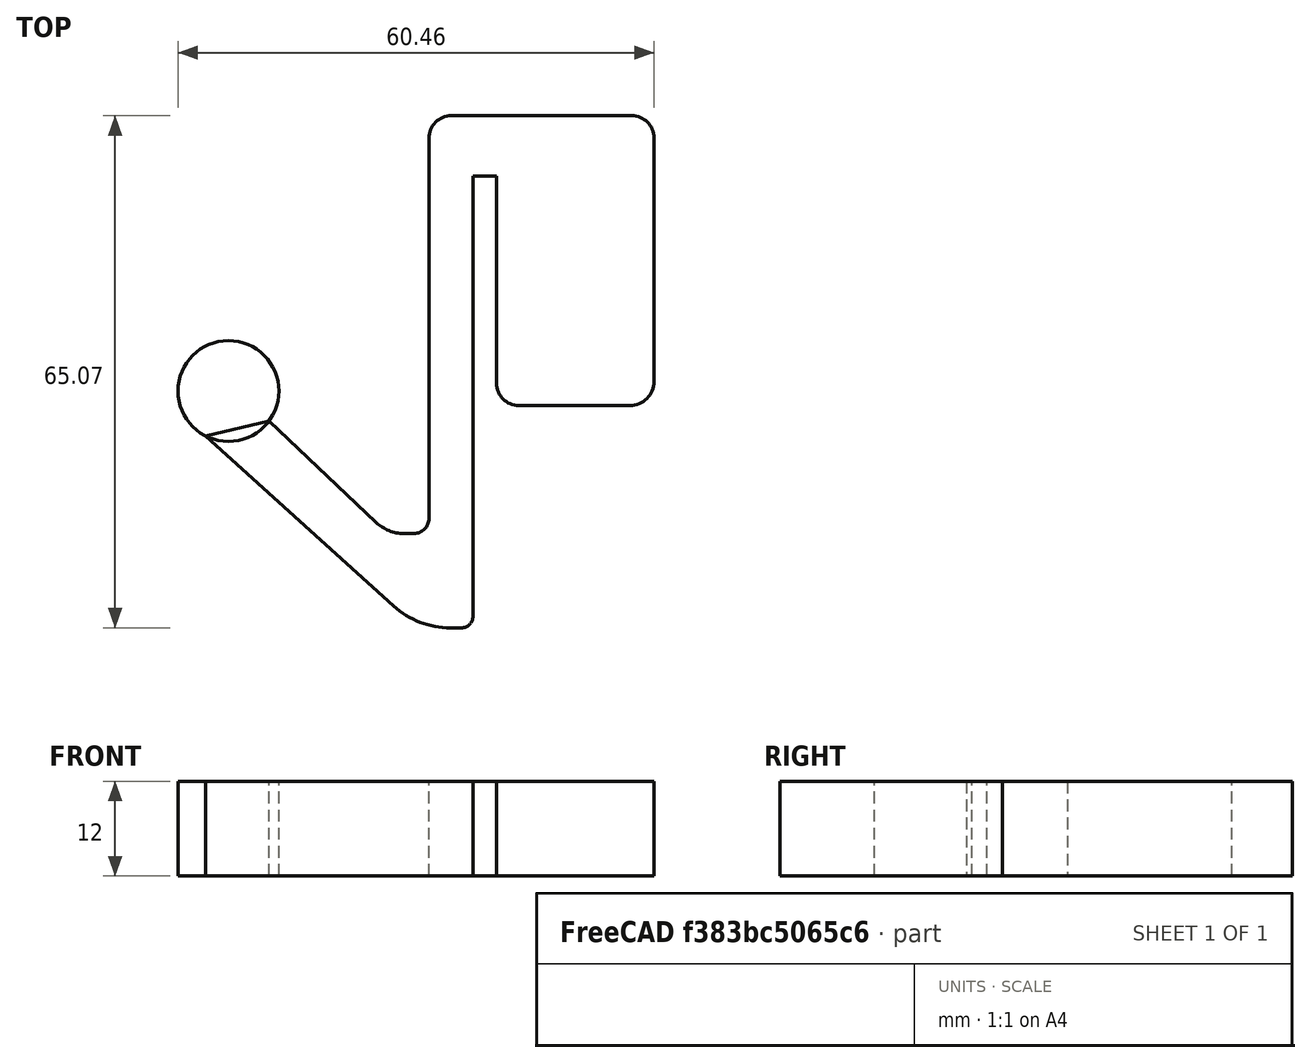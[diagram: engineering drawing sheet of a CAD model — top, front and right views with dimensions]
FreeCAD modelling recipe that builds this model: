
FCSTD DOCUMENT  (FreeCAD 0.14R3702 (Git))
Label: gancho_percha
License: CC-BY 3.0
LicenseURL: http://creativecommons.org/licenses/by/3.0/
objects: Sketcher::SketchObject×1, Part::Extrusion×1
note: 2 computed .brp shape members not serialized (recipe doc carries the construction recipe); baked Part::Feature solids carry a one-line shape summary decoded from their .brp

FEATURE [Sketcher::SketchObject] Sketch
  sketch-geometry (21):
    g0: LineSegment StartX=-5.72475 StartY=12.4254 StartZ=0 EndX=17.1762 EndY=12.4254 EndZ=0
    g1: LineSegment StartX=20 StartY=9.6016 StartZ=0 EndX=20 EndY=-21.3316 EndZ=0
    g2: LineSegment StartX=16.941 StartY=-24.3906 StartZ=0 EndX=2.83327 EndY=-24.3906 EndZ=0
    g3: LineSegment StartX=0 StartY=-21.5573 StartZ=0 EndX=0 EndY=4.75596 EndZ=0
    g4: LineSegment StartX=0 StartY=4.75596 StartZ=0 EndX=-3 EndY=4.75596 EndZ=0
    g5: LineSegment StartX=-3 StartY=4.75596 StartZ=0 EndX=-3 EndY=-51.1783 EndZ=0
    g6: LineSegment StartX=-4.46163 StartY=-52.64 StartZ=0 EndX=-5.86934 EndY=-52.64 EndZ=0
    g7: LineSegment StartX=-13.0633 StartY=-49.8689 StartZ=0 EndX=-36.9472 EndY=-28.2635 EndZ=0
    g8: LineSegment StartX=-36.9472 StartY=-28.2635 StartZ=0 EndX=-28.8858 EndY=-26.3305 EndZ=0
    g9: LineSegment StartX=-28.8858 StartY=-26.3305 StartZ=0 EndX=-15.2769 EndY=-39.2541 EndZ=0
    g10: LineSegment StartX=-11.7775 StartY=-40.651 StartZ=0 EndX=-10.4965 EndY=-40.651 EndZ=0
    g11: LineSegment StartX=-8.59039 StartY=-38.7449 StartZ=0 EndX=-8.59039 EndY=9.55975 EndZ=0
    g12: Circle CenterX=-34.0548 CenterY=-22.5498 CenterZ=0 NormalX=0 NormalY=0 NormalZ=1 Radius=6.40411
    g13: ArcOfCircle CenterX=-5.72475 CenterY=9.55975 CenterZ=0 NormalX=0 NormalY=0 NormalZ=1 Radius=2.86564 StartAngle=1.5708 EndAngle=3.14159
    g14: ArcOfCircle CenterX=17.1762 CenterY=9.6016 CenterZ=0 NormalX=0 NormalY=0 NormalZ=1 Radius=2.82379 StartAngle=0 EndAngle=1.5708
    g15: ArcOfCircle CenterX=2.83327 CenterY=-21.5573 CenterZ=0 NormalX=0 NormalY=0 NormalZ=1 Radius=2.83327 StartAngle=3.14159 EndAngle=4.71239
    g16: ArcOfCircle CenterX=16.941 CenterY=-21.3316 CenterZ=0 NormalX=0 NormalY=0 NormalZ=1 Radius=3.05903 StartAngle=4.71239 EndAngle=6.28319
    g17: ArcOfCircle CenterX=-11.7775 CenterY=-35.5692 CenterZ=0 NormalX=0 NormalY=0 NormalZ=1 Radius=5.08173 StartAngle=3.95281 EndAngle=4.71239
    g18: ArcOfCircle CenterX=-10.4965 CenterY=-38.7449 CenterZ=0 NormalX=0 NormalY=0 NormalZ=1 Radius=1.90609 StartAngle=4.71239 EndAngle=6.28319
    g19: ArcOfCircle CenterX=-5.86934 CenterY=-41.9163 CenterZ=0 NormalX=0 NormalY=0 NormalZ=1 Radius=10.7237 StartAngle=3.97704 EndAngle=4.71239
    g20: ArcOfCircle CenterX=-4.46163 CenterY=-51.1783 CenterZ=0 NormalX=0 NormalY=0 NormalZ=1 Radius=1.46163 StartAngle=4.71239 EndAngle=6.28319
  constraints (32):
    c: Horizontal(g0)
    c: Vertical(g1)
    c: Horizontal(g2)
    c: PointOnObject(g3,g-2)
    c: Coincident(g3,g4)
    c: Horizontal(g4)
    c: Coincident(g4,g5)
    c: Vertical(g5)
    c: Horizontal(g6)
    c: Coincident(g7,g8)
    c: Coincident(g8,g9)
    c: Horizontal(g10)
    c: Vertical(g11)
    c: PointOnObject(g7,g12)
    c: PointOnObject(g8,g12)
    c: DistanceX(g4) = -3
    c: Tangent(g11,g13)
    c: Tangent(g0,g13)
    c: Tangent(g0,g14)
    c: Tangent(g1,g14)
    c: Tangent(g3,g15)
    c: Tangent(g2,g15)
    c: Tangent(g2,g16)
    c: Tangent(g1,g16)
    c: Tangent(g9,g17)
    c: Tangent(g10,g17)
    c: Tangent(g10,g18)
    c: Tangent(g11,g18)
    c: Tangent(g7,g19)
    c: Tangent(g6,g19)
    c: Tangent(g6,g20)
    c: Tangent(g5,g20)
FEATURE [Part::Extrusion] Extrude
  Base = -> Sketch
  Dir = (0,0,12)
  Solid = true
